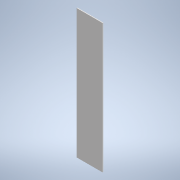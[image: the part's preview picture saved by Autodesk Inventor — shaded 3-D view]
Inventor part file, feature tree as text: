
AUTODESK INVENTOR PART (.ipt)
format: ipt  version: 2022 (Build 260153000, 153)  size: 91,136 bytes
history: native  units: in
note: dims shown in document units (in); Inventor stores cm internally (conversion verified against a paired STEP export)
features: extrude x1, sketch x1
ambient origin geometry x8: Origin, YZ Plane, XZ Plane, XY Plane, X Axis, Y Axis, Z Axis, Center Point
bodies: Solid1 (feature_tree)
feature tree (2):
  extrude  "Extrusion1"  [1 undecoded]
  sketch  "Sketch1"  dims[d0=0.2362in d1=0.0in]
note: 1 required parameter value undecoded (feature->parameter linkage not recoverable at this tier; creation-order binding heuristic only, values carry confidence <= 0.55)
